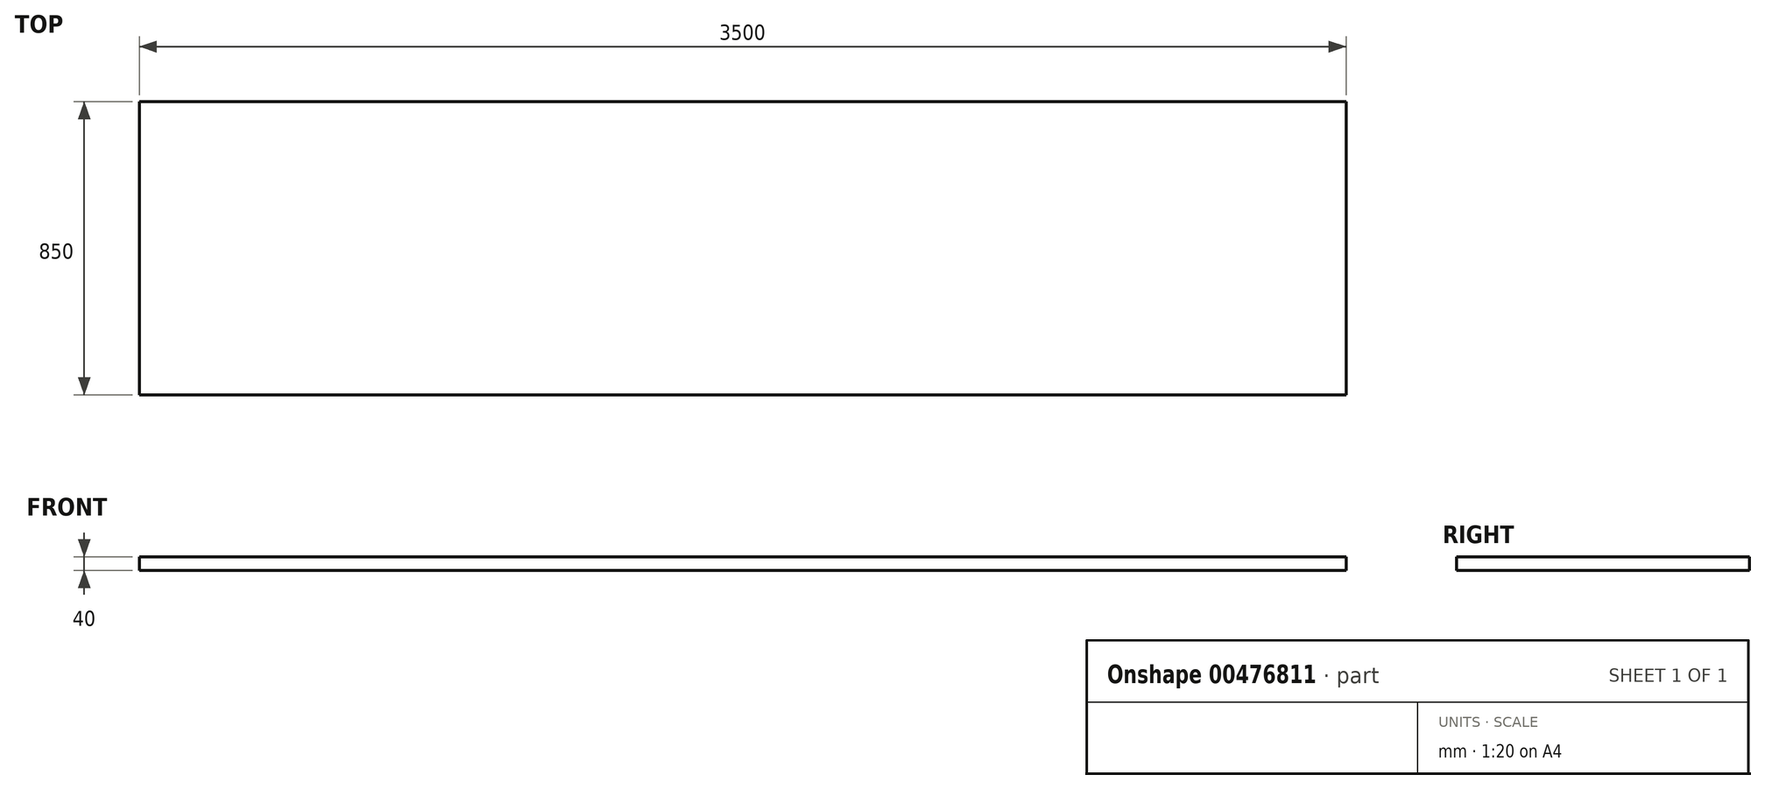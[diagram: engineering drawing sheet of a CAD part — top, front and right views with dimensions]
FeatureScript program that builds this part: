
annotation { "Feature Type Name" : "Feature", "Feature Type Description" : "" }
export const myFeature = defineFeature(function(context is Context, id is Id, definition is map)
    precondition{}
    {
        {
            var Q0;
            Q0=qCreatedBy(makeId("Top.planeOp"),FACE);
            var sketch = newSketch(context, id + "F0", { "sketchPlane" : qUnion([Q0])});
            skLineSegment(sketch, "E0", {"start": v(-1754.32, -941.75) * mm, "end": v(-1754.32, -91.75) * mm});
            skLineSegment(sketch, "E1", {"start": v(-1754.32, -91.75) * mm, "end": v(1745.68, -91.75) * mm});
            skLineSegment(sketch, "E2", {"start": v(1745.68, -91.75) * mm, "end": v(1745.68, -941.75) * mm});
            skLineSegment(sketch, "E3", {"start": v(1745.68, -941.75) * mm, "end": v(-1754.32, -941.75) * mm});
            skSolve(sketch);
        }
        {
            var Q0;
            Q0=makeQuery(id+"F0.imprint","IMPRINT",FACE,{"disambiguationData":[TD([[makeQuery(id+"F0.imprint","IMPRINT",EDGE,{"derivedFrom":sQuery(id+"F0.wireOp",EDGE,"E0")}),-1.0]])]});
            extrude(context, id + "F1", {"entities" : qUnion([Q0]), "endBound" : BoundingType.SYMMETRIC, "depth" : 40 * mm});
        }
    });
